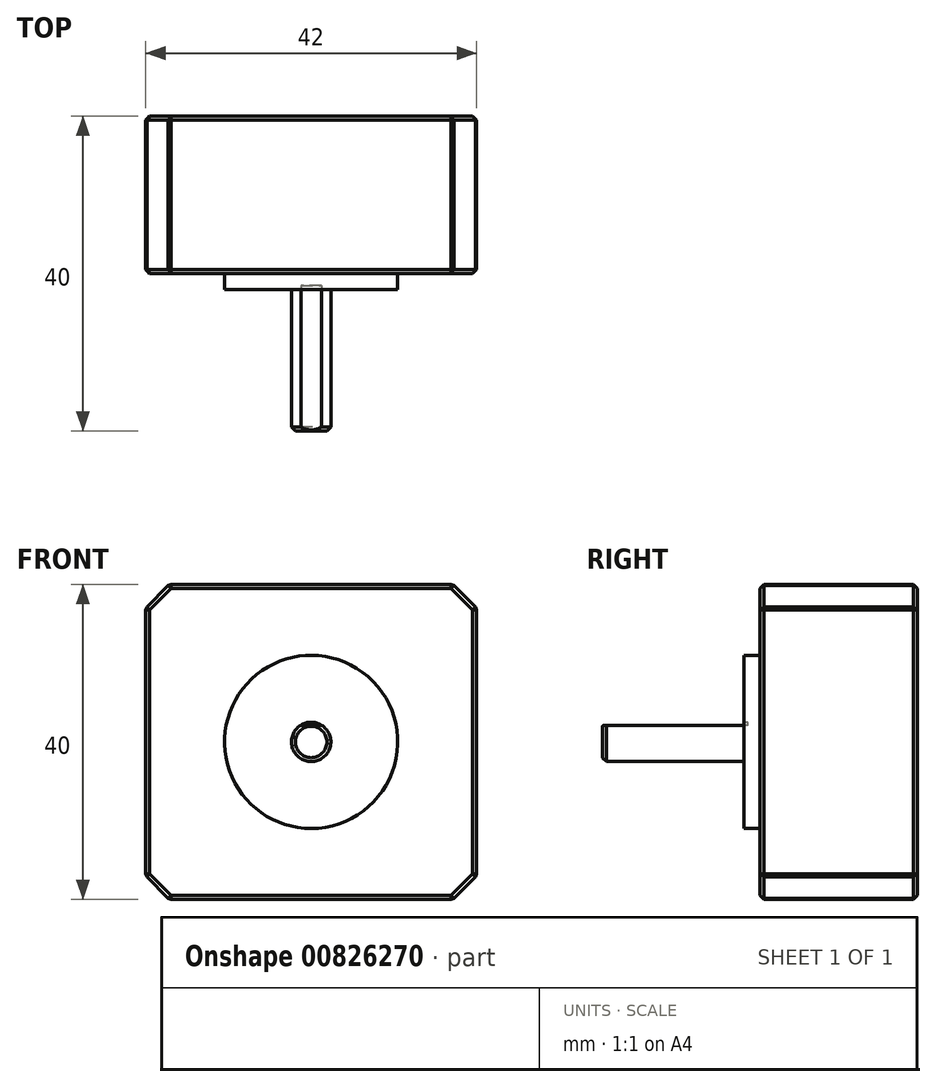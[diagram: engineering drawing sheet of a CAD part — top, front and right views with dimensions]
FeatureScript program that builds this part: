
annotation { "Feature Type Name" : "Feature", "Feature Type Description" : "" }
export const myFeature = defineFeature(function(context is Context, id is Id, definition is map)
    precondition{}
    {
        {
            var Q0;
            Q0=qCreatedBy(makeId("Front.planeOp"),FACE);
            var sketch = newSketch(context, id + "F0", { "sketchPlane" : qUnion([Q0])});
            skCircle(sketch, "E0", {"center": v(0, 0) * mm, "radius": 2.5 * mm});
            skLineSegment(sketch, "E1", {"start": v(-1.31, 2.13) * mm, "end": v(1.31, 2.13) * mm});
            skCircle(sketch, "E2", {"center": v(0, 0) * mm, "radius": 11 * mm});
            skLineSegment(sketch, "E3", {"start": v(-21, 0) * mm, "end": v(-21, 15.5) * mm});
            skLineSegment(sketch, "E4", {"start": v(-21, 15.5) * mm, "end": v(-15.5, 21) * mm});
            skLineSegment(sketch, "E5", {"start": v(-15.5, 21) * mm, "end": v(0, 21) * mm});
            skLineSegment(sketch, "E6", {"start": v(0, 0) * mm, "end": v(-21, 0) * mm, "construction": true});
            skLineSegment(sketch, "E7", {"start": v(0, 0) * mm, "end": v(0, 21) * mm, "construction": true});
            skCircle(sketch, "E8", {"center": v(-15.7, 15.69) * mm, "radius": 1.5 * mm});
            skLineSegment(sketch, "E9.MirrorCS", {"start": v(15.5, 21) * mm, "end": v(0, 21) * mm});
            skLineSegment(sketch, "E10.MirrorCS", {"start": v(21, 15.5) * mm, "end": v(15.5, 21) * mm});
            skLineSegment(sketch, "E11.MirrorCS", {"start": v(21, 0) * mm, "end": v(21, 15.5) * mm});
            skCircle(sketch, "E12.MirrorC", {"center": v(15.7, 15.69) * mm, "radius": 1.5 * mm});
            skLineSegment(sketch, "E13", {"start": v(0, 0) * mm, "end": v(21, 0) * mm, "construction": true});
            skLineSegment(sketch, "E14.MirrorCS", {"start": v(15.5, -21) * mm, "end": v(0, -21) * mm});
            skLineSegment(sketch, "E15.MirrorCS", {"start": v(21, -15.5) * mm, "end": v(15.5, -21) * mm});
            skLineSegment(sketch, "E16.MirrorCS", {"start": v(21, 0) * mm, "end": v(21, -15.5) * mm});
            skCircle(sketch, "E17.MirrorC", {"center": v(15.7, -15.69) * mm, "radius": 1.5 * mm});
            skLineSegment(sketch, "E18", {"start": v(0, -21) * mm, "end": v(0, 0) * mm, "construction": true});
            skLineSegment(sketch, "E19.MirrorCS", {"start": v(-21, 0) * mm, "end": v(-21, -15.5) * mm});
            skLineSegment(sketch, "E20.MirrorCS", {"start": v(-21, -15.5) * mm, "end": v(-15.5, -21) * mm});
            skLineSegment(sketch, "E21.MirrorCS", {"start": v(-15.5, -21) * mm, "end": v(0, -21) * mm});
            skCircle(sketch, "E22.MirrorC", {"center": v(-15.7, -15.69) * mm, "radius": 1.5 * mm});
            skLineSegment(sketch, "E23", {"start": v(0, -21.57) * mm, "end": v(0, -21) * mm});
            skLineSegment(sketch, "E24", {"start": v(0, -21.57) * mm, "end": v(-2.98, -21.57) * mm});
            skLineSegment(sketch, "E25", {"start": v(-2.98, -21.57) * mm, "end": v(-2.98, -21) * mm});
            skLineSegment(sketch, "E26", {"start": v(-2, -21.57) * mm, "end": v(-2, -29.07) * mm});
            skLineSegment(sketch, "E27", {"start": v(-2, -29.07) * mm, "end": v(-1, -29.07) * mm});
            skLineSegment(sketch, "E28", {"start": v(-1, -29.07) * mm, "end": v(-1, -21.57) * mm});
            skLineSegment(sketch, "E29", {"start": v(-1, -21.57) * mm, "end": v(0, -21.57) * mm});
            skLineSegment(sketch, "E30", {"start": v(0, -21.57) * mm, "end": v(0, -29.1) * mm});
            skLineSegment(sketch, "E31", {"start": v(0, -29.1) * mm, "end": v(-1, -29.07) * mm});
            skLineSegment(sketch, "E32.MirrorCS", {"start": v(2, -21.57) * mm, "end": v(2, -29.07) * mm});
            skLineSegment(sketch, "E33.MirrorCS", {"start": v(1, -29.07) * mm, "end": v(1, -21.57) * mm});
            skLineSegment(sketch, "E34.MirrorCS", {"start": v(2, -29.07) * mm, "end": v(1, -29.07) * mm});
            skLineSegment(sketch, "E35.MirrorCS", {"start": v(0, -29.1) * mm, "end": v(1, -29.07) * mm});
            skLineSegment(sketch, "E36.MirrorCS", {"start": v(0, -21.57) * mm, "end": v(2.98, -21.57) * mm});
            skLineSegment(sketch, "E37.MirrorCS", {"start": v(2.98, -21.57) * mm, "end": v(2.98, -21) * mm});
            skLineSegment(sketch, "E38", {"start": v(0, 0) * mm, "end": v(0, 11) * mm});
            skLineSegment(sketch, "E39", {"start": v(0, 0) * mm, "end": v(0, -2.5) * mm});
            skLineSegment(sketch, "E40", {"start": v(0, 0) * mm, "end": v(-1.31, 2.13) * mm, "construction": true});
            skLineSegment(sketch, "E41", {"start": v(0, 0) * mm, "end": v(1.31, 2.13) * mm, "construction": true});
            skSolve(sketch);
        }
        {
            var Q0;
            Q0=qCreatedBy(makeId("Right.planeOp"),FACE);
            var sketch = newSketch(context, id + "F1", { "sketchPlane" : qUnion([Q0])});
            skLineSegment(sketch, "E42", {"start": v(-6.62, 2.5) * mm, "end": v(-24.6, 2.5) * mm});
            skLineSegment(sketch, "E43", {"start": v(-24.6, 2.5) * mm, "end": v(-24.6, 0) * mm});
            skLineSegment(sketch, "E44", {"start": v(-24.6, -2.5) * mm, "end": v(-6.62, -2.5) * mm});
            skLineSegment(sketch, "E45", {"start": v(-6.62, 2.5) * mm, "end": v(-6.62, 0) * mm});
            skLineSegment(sketch, "E46", {"start": v(0, 0) * mm, "end": v(-24.6, 0) * mm, "construction": true});
            skLineSegment(sketch, "E47", {"start": v(-4.6, 20) * mm, "end": v(15.4, 20) * mm});
            skLineSegment(sketch, "E48", {"start": v(-6.6, 11) * mm, "end": v(-4.6, 11) * mm});
            skLineSegment(sketch, "E49", {"start": v(-6.6, 11) * mm, "end": v(-6.62, 2.5) * mm});
            skLineSegment(sketch, "E50", {"start": v(-4.6, 20) * mm, "end": v(-4.6, 11) * mm});
            skLineSegment(sketch, "E51", {"start": v(1, 20) * mm, "end": v(1, 13.33) * mm});
            skLineSegment(sketch, "E52", {"start": v(9.34, 20) * mm, "end": v(9.34, 13.33) * mm});
            skLineSegment(sketch, "E53", {"start": v(1, 13.33) * mm, "end": v(9.34, 13.33) * mm});
            skLineSegment(sketch, "E54", {"start": v(15.4, 0) * mm, "end": v(15.4, 20) * mm});
            skLineSegment(sketch, "E55", {"start": v(-4.6, 9.38) * mm, "end": v(1, 9.38) * mm});
            skLineSegment(sketch, "E56", {"start": v(1, 9.38) * mm, "end": v(9.34, 9.38) * mm, "construction": true});
            skLineSegment(sketch, "E57", {"start": v(9.34, 9.38) * mm, "end": v(15.4, 9.38) * mm});
            skLineSegment(sketch, "E58", {"start": v(-4.6, 11) * mm, "end": v(-4.6, 0) * mm});
            skLineSegment(sketch, "E59", {"start": v(0, 13.33) * mm, "end": v(1, 13.33) * mm});
            skLineSegment(sketch, "E60", {"start": v(0, 0) * mm, "end": v(0, 13.33) * mm});
            skLineSegment(sketch, "E61", {"start": v(9.34, 13.33) * mm, "end": v(10.34, 13.33) * mm});
            skLineSegment(sketch, "E62", {"start": v(10.34, 13.33) * mm, "end": v(10.34, 0) * mm});
            skLineSegment(sketch, "E63", {"start": v(-24.6, 0) * mm, "end": v(-24.6, -2.5) * mm});
            skLineSegment(sketch, "E64", {"start": v(-6.62, 0) * mm, "end": v(-6.62, -2.5) * mm});
            skLineSegment(sketch, "E65", {"start": v(-24.6, 0) * mm, "end": v(-6.62, 0) * mm});
            skLineSegment(sketch, "E66", {"start": v(10.34, 0) * mm, "end": v(15.4, 0) * mm});
            skLineSegment(sketch, "E67", {"start": v(-6.62, 0) * mm, "end": v(-4.6, 0) * mm});
            skLineSegment(sketch, "E68", {"start": v(0, 0) * mm, "end": v(10.34, 0) * mm});
            skLineSegment(sketch, "E69", {"start": v(-4.6, 0) * mm, "end": v(0, 0) * mm});
            skLineSegment(sketch, "E70.MirrorCS", {"start": v(-4.6, -11) * mm, "end": v(-4.6, 0) * mm});
            skLineSegment(sketch, "E71.MirrorCS", {"start": v(-4.6, -20) * mm, "end": v(-4.6, -11) * mm});
            skLineSegment(sketch, "E72.MirrorCS", {"start": v(-4.6, -9.38) * mm, "end": v(1, -9.38) * mm});
            skLineSegment(sketch, "E73.MirrorCS", {"start": v(-4.6, -20) * mm, "end": v(15.4, -20) * mm});
            skLineSegment(sketch, "E74.MirrorCS", {"start": v(1, -20) * mm, "end": v(1, -13.33) * mm});
            skLineSegment(sketch, "E75.MirrorCS", {"start": v(1, -9.38) * mm, "end": v(9.34, -9.38) * mm, "construction": true});
            skLineSegment(sketch, "E76.MirrorCS", {"start": v(1, -13.33) * mm, "end": v(9.34, -13.33) * mm});
            skLineSegment(sketch, "E77.MirrorCS", {"start": v(0, -13.33) * mm, "end": v(1, -13.33) * mm});
            skLineSegment(sketch, "E78.MirrorCS", {"start": v(0, 0) * mm, "end": v(0, -13.33) * mm});
            skLineSegment(sketch, "E79.MirrorCS", {"start": v(9.34, -13.33) * mm, "end": v(10.34, -13.33) * mm});
            skLineSegment(sketch, "E80.MirrorCS", {"start": v(10.34, -13.33) * mm, "end": v(10.34, 0) * mm});
            skLineSegment(sketch, "E81.MirrorCS", {"start": v(9.34, -20) * mm, "end": v(9.34, -13.33) * mm});
            skLineSegment(sketch, "E82.MirrorCS", {"start": v(9.34, -9.38) * mm, "end": v(15.4, -9.38) * mm});
            skLineSegment(sketch, "E83.MirrorCS", {"start": v(15.4, 0) * mm, "end": v(15.4, -20) * mm});
            skSolve(sketch);
        }
        {
            var Q0;
            Q0=makeQuery(id+"F1.imprint","IMPRINT",FACE,{"disambiguationData":[TD([[makeQuery(id+"F1.imprint","IMPRINT",EDGE,{"derivedFrom":sQuery(id+"F1.wireOp",EDGE,"E42")}),1.0]])]});
            var Q1;
            Q1=makeQuery(id+"F1.imprint","IMPRINT",FACE,{"disambiguationData":[TD([[makeQuery(id+"F1.imprint","IMPRINT",EDGE,{"derivedFrom":sQuery(id+"F1.wireOp",EDGE,"E45")}),1.0]])]});
            var Q2;
            Q2=sQuery(id+"F1.wireOp",EDGE,"E65");
            revolve(context, id + "F2", {"surfaceOperationType" : NewSurfaceOperationType.NEW, "entities" : qUnion([Q0, Q1]), "axis" : qUnion([Q2]), "revolveType" : RevolveType.FULL});
        }
        {
            var Q0;
            {var subQ0=sQuery(id+"F1.wireOp",EDGE,"E55");Q0=makeQuery(id+"F1.imprint","IMPRINT",FACE,{"disambiguationData":[TD([[makeQuery(id+"F1.imprint","IMPRINT",EDGE,{"derivedFrom":subQ0}),-1.0]])]});}
            var Q1;
            {var subQ5=sQuery(id+"F1.wireOp",EDGE,"E55");Q1=makeQuery(id+"F1.imprint","IMPRINT",FACE,{"disambiguationData":[TD([[makeQuery(id+"F1.imprint","IMPRINT",EDGE,{"derivedFrom":subQ5}),1.0]])]});}
            var Q2;
            {var subQ4=sQuery(id+"F1.wireOp",EDGE,"E53");Q2=makeQuery(id+"F1.imprint","IMPRINT",FACE,{"disambiguationData":[TD([[makeQuery(id+"F1.imprint","IMPRINT",EDGE,{"derivedFrom":subQ4}),1.0]])]});}
            var Q3;
            Q3=makeQuery(id+"F1.imprint","IMPRINT",FACE,{"disambiguationData":[TD([[makeQuery(id+"F1.imprint","IMPRINT",EDGE,{"derivedFrom":sQuery(id+"F1.wireOp",EDGE,"E53")}),-1.0]])]});
            var Q4;
            {var subQ3=sQuery(id+"F1.wireOp",EDGE,"E57");Q4=makeQuery(id+"F1.imprint","IMPRINT",FACE,{"disambiguationData":[TD([[makeQuery(id+"F1.imprint","IMPRINT",EDGE,{"derivedFrom":subQ3}),-1.0]])]});}
            var Q5;
            {var subQ5=sQuery(id+"F1.wireOp",EDGE,"E57");Q5=makeQuery(id+"F1.imprint","IMPRINT",FACE,{"disambiguationData":[TD([[makeQuery(id+"F1.imprint","IMPRINT",EDGE,{"derivedFrom":subQ5}),1.0]])]});}
            var Q6;
            Q6=makeQuery(id+"F1.imprint","IMPRINT",FACE,{"disambiguationData":[TD([[makeQuery(id+"F1.imprint","IMPRINT",EDGE,{"derivedFrom":sQuery(id+"F1.wireOp",EDGE,"E69")}),-1.0]])]});
            var Q7;
            Q7=makeQuery(id+"F1.imprint","IMPRINT",FACE,{"disambiguationData":[TD([[makeQuery(id+"F1.imprint","IMPRINT",EDGE,{"derivedFrom":sQuery(id+"F1.wireOp",EDGE,"E68")}),-1.0]])]});
            var Q8;
            {var subQ6=sQuery(id+"F1.wireOp",EDGE,"E76.MirrorCS");Q8=makeQuery(id+"F1.imprint","IMPRINT",FACE,{"disambiguationData":[TD([[makeQuery(id+"F1.imprint","IMPRINT",EDGE,{"derivedFrom":subQ6}),-1.0]])]});}
            var Q9;
            {var subQ3=sQuery(id+"F1.wireOp",EDGE,"E66");Q9=makeQuery(id+"F1.imprint","IMPRINT",FACE,{"disambiguationData":[TD([[makeQuery(id+"F1.imprint","IMPRINT",EDGE,{"derivedFrom":subQ3}),-1.0]])]});}
            var Q10;
            {var subQ5=sQuery(id+"F1.wireOp",EDGE,"E82.MirrorCS");Q10=makeQuery(id+"F1.imprint","IMPRINT",FACE,{"disambiguationData":[TD([[makeQuery(id+"F1.imprint","IMPRINT",EDGE,{"derivedFrom":subQ5}),-1.0]])]});}
            var Q11;
            {var subQ3=sQuery(id+"F1.wireOp",EDGE,"E72.MirrorCS");Q11=makeQuery(id+"F1.imprint","IMPRINT",FACE,{"disambiguationData":[TD([[makeQuery(id+"F1.imprint","IMPRINT",EDGE,{"derivedFrom":subQ3}),-1.0]])]});}
            extrude(context, id + "F3", {"entities" : qUnion([Q0, Q1, Q2, Q3, Q4, Q5, Q6, Q7, Q8, Q9, Q10, Q11]), "operationType" : NewBodyOperationType.ADD, "endBound" : BoundingType.SYMMETRIC, "depth" : 42 * mm, "offsetDistance" : 25 * mm});
        }
        {
            var Q0;
            Q0=makeQuery(id+"F3.opExtrude","CAP_EDGE",EDGE,{"disambiguationData":[OSD([sQuery(id+"F1.wireOp",EDGE,"E47")])],"isStart":true});
            var Q1;
            Q1=makeQuery(id+"F3.opExtrude","CAP_EDGE",EDGE,{"disambiguationData":[OSD([sQuery(id+"F1.wireOp",EDGE,"E47")])],"isStart":false});
            var Q2;
            Q2=makeQuery(id+"F3.opExtrude","CAP_EDGE",EDGE,{"disambiguationData":[OSD([sQuery(id+"F1.wireOp",EDGE,"E73.MirrorCS")])],"isStart":true});
            var Q3;
            Q3=makeQuery(id+"F3.opExtrude","CAP_EDGE",EDGE,{"disambiguationData":[OSD([sQuery(id+"F1.wireOp",EDGE,"E73.MirrorCS")])],"isStart":false});
            chamfer(context, id + "F4", {"entities" : qUnion([Q0, Q1, Q2, Q3]), "width" : 3 * mm, "tangentPropagation" : true});
        }
        {
            var Q0;
            Q0=makeQuery(id+"F3.opExtrude","SWEPT_EDGE",EDGE,{"disambiguationData":[OSD([sQuery(id+"F1.wireOp",EDGE,"E47"),sQuery(id+"F1.wireOp",EDGE,"E50")])]});
            var Q1;
            Q1=makeQuery(id+"F4.opChamfer","BLEND_EDGE",EDGE,{"blendedFrom":[makeQuery(id+"F3.opExtrude","CAP_EDGE",EDGE,{"disambiguationData":[OSD([sQuery(id+"F1.wireOp",EDGE,"E47")])],"isStart":false}),makeQuery(id+"F3.opExtrude","SWEPT_FACE",FACE,{"disambiguationData":[OSD([sQuery(id+"F1.wireOp",EDGE,"E50"),sQuery(id+"F1.wireOp",EDGE,"E58"),sQuery(id+"F1.wireOp",EDGE,"E70.MirrorCS"),sQuery(id+"F1.wireOp",EDGE,"E71.MirrorCS")])]})],"blendedInto":[makeQuery(id+"F3.opExtrude","SWEPT_FACE",FACE,{"disambiguationData":[OSD([sQuery(id+"F1.wireOp",EDGE,"E50"),sQuery(id+"F1.wireOp",EDGE,"E58"),sQuery(id+"F1.wireOp",EDGE,"E70.MirrorCS"),sQuery(id+"F1.wireOp",EDGE,"E71.MirrorCS")])]})]});
            var Q2;
            Q2=makeQuery(id+"F3.opExtrude","CAP_EDGE",EDGE,{"disambiguationData":[OSD([sQuery(id+"F1.wireOp",EDGE,"E50"),sQuery(id+"F1.wireOp",EDGE,"E58"),sQuery(id+"F1.wireOp",EDGE,"E70.MirrorCS"),sQuery(id+"F1.wireOp",EDGE,"E71.MirrorCS")])],"isStart":false});
            var Q3;
            Q3=makeQuery(id+"F4.opChamfer","BLEND_EDGE",EDGE,{"blendedFrom":[makeQuery(id+"F3.opExtrude","CAP_EDGE",EDGE,{"disambiguationData":[OSD([sQuery(id+"F1.wireOp",EDGE,"E73.MirrorCS")])],"isStart":false}),makeQuery(id+"F3.opExtrude","SWEPT_FACE",FACE,{"disambiguationData":[OSD([sQuery(id+"F1.wireOp",EDGE,"E50"),sQuery(id+"F1.wireOp",EDGE,"E58"),sQuery(id+"F1.wireOp",EDGE,"E70.MirrorCS"),sQuery(id+"F1.wireOp",EDGE,"E71.MirrorCS")])]})],"blendedInto":[makeQuery(id+"F3.opExtrude","SWEPT_FACE",FACE,{"disambiguationData":[OSD([sQuery(id+"F1.wireOp",EDGE,"E50"),sQuery(id+"F1.wireOp",EDGE,"E58"),sQuery(id+"F1.wireOp",EDGE,"E70.MirrorCS"),sQuery(id+"F1.wireOp",EDGE,"E71.MirrorCS")])]})]});
            var Q4;
            Q4=makeQuery(id+"F3.opExtrude","SWEPT_EDGE",EDGE,{"disambiguationData":[OSD([sQuery(id+"F1.wireOp",EDGE,"E71.MirrorCS"),sQuery(id+"F1.wireOp",EDGE,"E73.MirrorCS")])]});
            var Q5;
            Q5=makeQuery(id+"F3.opExtrude","CAP_EDGE",EDGE,{"disambiguationData":[OSD([sQuery(id+"F1.wireOp",EDGE,"E50"),sQuery(id+"F1.wireOp",EDGE,"E58"),sQuery(id+"F1.wireOp",EDGE,"E70.MirrorCS"),sQuery(id+"F1.wireOp",EDGE,"E71.MirrorCS")])],"isStart":true});
            var Q6;
            Q6=makeQuery(id+"F4.opChamfer","BLEND_EDGE",EDGE,{"blendedFrom":[makeQuery(id+"F3.opExtrude","CAP_EDGE",EDGE,{"disambiguationData":[OSD([sQuery(id+"F1.wireOp",EDGE,"E47")])],"isStart":true}),makeQuery(id+"F3.opExtrude","SWEPT_FACE",FACE,{"disambiguationData":[OSD([sQuery(id+"F1.wireOp",EDGE,"E50"),sQuery(id+"F1.wireOp",EDGE,"E58"),sQuery(id+"F1.wireOp",EDGE,"E70.MirrorCS"),sQuery(id+"F1.wireOp",EDGE,"E71.MirrorCS")])]})],"blendedInto":[makeQuery(id+"F3.opExtrude","SWEPT_FACE",FACE,{"disambiguationData":[OSD([sQuery(id+"F1.wireOp",EDGE,"E50"),sQuery(id+"F1.wireOp",EDGE,"E58"),sQuery(id+"F1.wireOp",EDGE,"E70.MirrorCS"),sQuery(id+"F1.wireOp",EDGE,"E71.MirrorCS")])]})]});
            var Q7;
            Q7=makeQuery(id+"F3.opExtrude","CAP_EDGE",EDGE,{"disambiguationData":[OSD([sQuery(id+"F1.wireOp",EDGE,"E54"),sQuery(id+"F1.wireOp",EDGE,"E83.MirrorCS")])],"isStart":false});
            var Q8;
            Q8=makeQuery(id+"F4.opChamfer","BLEND_EDGE",EDGE,{"blendedFrom":[makeQuery(id+"F3.opExtrude","CAP_EDGE",EDGE,{"disambiguationData":[OSD([sQuery(id+"F1.wireOp",EDGE,"E47")])],"isStart":false}),makeQuery(id+"F3.opExtrude","SWEPT_FACE",FACE,{"disambiguationData":[OSD([sQuery(id+"F1.wireOp",EDGE,"E54"),sQuery(id+"F1.wireOp",EDGE,"E83.MirrorCS")])]})],"blendedInto":[makeQuery(id+"F3.opExtrude","SWEPT_FACE",FACE,{"disambiguationData":[OSD([sQuery(id+"F1.wireOp",EDGE,"E54"),sQuery(id+"F1.wireOp",EDGE,"E83.MirrorCS")])]})]});
            var Q9;
            Q9=makeQuery(id+"F3.opExtrude","SWEPT_EDGE",EDGE,{"disambiguationData":[OSD([sQuery(id+"F1.wireOp",EDGE,"E47"),sQuery(id+"F1.wireOp",EDGE,"E54")])]});
            var Q10;
            Q10=makeQuery(id+"F4.opChamfer","BLEND_EDGE",EDGE,{"blendedFrom":[makeQuery(id+"F3.opExtrude","CAP_EDGE",EDGE,{"disambiguationData":[OSD([sQuery(id+"F1.wireOp",EDGE,"E47")])],"isStart":true}),makeQuery(id+"F3.opExtrude","SWEPT_FACE",FACE,{"disambiguationData":[OSD([sQuery(id+"F1.wireOp",EDGE,"E54"),sQuery(id+"F1.wireOp",EDGE,"E83.MirrorCS")])]})],"blendedInto":[makeQuery(id+"F3.opExtrude","SWEPT_FACE",FACE,{"disambiguationData":[OSD([sQuery(id+"F1.wireOp",EDGE,"E54"),sQuery(id+"F1.wireOp",EDGE,"E83.MirrorCS")])]})]});
            var Q11;
            Q11=makeQuery(id+"F3.opExtrude","CAP_EDGE",EDGE,{"disambiguationData":[OSD([sQuery(id+"F1.wireOp",EDGE,"E54"),sQuery(id+"F1.wireOp",EDGE,"E83.MirrorCS")])],"isStart":true});
            var Q12;
            Q12=makeQuery(id+"F4.opChamfer","BLEND_EDGE",EDGE,{"blendedFrom":[makeQuery(id+"F3.opExtrude","CAP_EDGE",EDGE,{"disambiguationData":[OSD([sQuery(id+"F1.wireOp",EDGE,"E73.MirrorCS")])],"isStart":true}),makeQuery(id+"F3.opExtrude","SWEPT_FACE",FACE,{"disambiguationData":[OSD([sQuery(id+"F1.wireOp",EDGE,"E54"),sQuery(id+"F1.wireOp",EDGE,"E83.MirrorCS")])]})],"blendedInto":[makeQuery(id+"F3.opExtrude","SWEPT_FACE",FACE,{"disambiguationData":[OSD([sQuery(id+"F1.wireOp",EDGE,"E54"),sQuery(id+"F1.wireOp",EDGE,"E83.MirrorCS")])]})]});
            var Q13;
            Q13=makeQuery(id+"F3.opExtrude","SWEPT_EDGE",EDGE,{"disambiguationData":[OSD([sQuery(id+"F1.wireOp",EDGE,"E73.MirrorCS"),sQuery(id+"F1.wireOp",EDGE,"E83.MirrorCS")])]});
            var Q14;
            Q14=makeQuery(id+"F4.opChamfer","BLEND_EDGE",EDGE,{"blendedFrom":[makeQuery(id+"F3.opExtrude","CAP_EDGE",EDGE,{"disambiguationData":[OSD([sQuery(id+"F1.wireOp",EDGE,"E73.MirrorCS")])],"isStart":false}),makeQuery(id+"F3.opExtrude","SWEPT_FACE",FACE,{"disambiguationData":[OSD([sQuery(id+"F1.wireOp",EDGE,"E54"),sQuery(id+"F1.wireOp",EDGE,"E83.MirrorCS")])]})],"blendedInto":[makeQuery(id+"F3.opExtrude","SWEPT_FACE",FACE,{"disambiguationData":[OSD([sQuery(id+"F1.wireOp",EDGE,"E54"),sQuery(id+"F1.wireOp",EDGE,"E83.MirrorCS")])]})]});
            var Q15;
            {var subQ0=sQuery(id+"F1.wireOp",EDGE,"E73.MirrorCS");Q15=makeQuery(id+"F4.opChamfer","BLEND_EDGE",EDGE,{"blendedFrom":[makeQuery(id+"F3.opExtrude","CAP_EDGE",EDGE,{"disambiguationData":[OSD([subQ0])],"isStart":false}),makeQuery(id+"F3.opExtrude","CAP_FACE",FACE,{"disambiguationData":[OSD([sQuery(id+"F1.wireOp",EDGE,"E47"),sQuery(id+"F1.wireOp",EDGE,"E50"),sQuery(id+"F1.wireOp",EDGE,"E54"),sQuery(id+"F1.wireOp",EDGE,"E58"),sQuery(id+"F1.wireOp",EDGE,"E70.MirrorCS"),sQuery(id+"F1.wireOp",EDGE,"E71.MirrorCS"),subQ0,sQuery(id+"F1.wireOp",EDGE,"E83.MirrorCS")])],"isStart":false})],"blendedInto":[makeQuery(id+"F3.opExtrude","CAP_FACE",FACE,{"disambiguationData":[OSD([sQuery(id+"F1.wireOp",EDGE,"E47"),sQuery(id+"F1.wireOp",EDGE,"E50"),sQuery(id+"F1.wireOp",EDGE,"E54"),sQuery(id+"F1.wireOp",EDGE,"E58"),sQuery(id+"F1.wireOp",EDGE,"E70.MirrorCS"),sQuery(id+"F1.wireOp",EDGE,"E71.MirrorCS"),subQ0,sQuery(id+"F1.wireOp",EDGE,"E83.MirrorCS")])],"isStart":false})]});}
            var Q16;
            {var subQ0=sQuery(id+"F1.wireOp",EDGE,"E73.MirrorCS");Q16=makeQuery(id+"F4.opChamfer","BLEND_EDGE",EDGE,{"blendedFrom":[makeQuery(id+"F3.opExtrude","CAP_EDGE",EDGE,{"disambiguationData":[OSD([subQ0])],"isStart":false}),makeQuery(id+"F3.opExtrude","SWEPT_FACE",FACE,{"disambiguationData":[OSD([subQ0])]})],"blendedInto":[makeQuery(id+"F3.opExtrude","SWEPT_FACE",FACE,{"disambiguationData":[OSD([subQ0])]})]});}
            var Q17;
            {var subQ0=sQuery(id+"F1.wireOp",EDGE,"E47");Q17=makeQuery(id+"F4.opChamfer","BLEND_EDGE",EDGE,{"blendedFrom":[makeQuery(id+"F3.opExtrude","CAP_EDGE",EDGE,{"disambiguationData":[OSD([subQ0])],"isStart":false}),makeQuery(id+"F3.opExtrude","CAP_FACE",FACE,{"disambiguationData":[OSD([subQ0,sQuery(id+"F1.wireOp",EDGE,"E50"),sQuery(id+"F1.wireOp",EDGE,"E54"),sQuery(id+"F1.wireOp",EDGE,"E58"),sQuery(id+"F1.wireOp",EDGE,"E70.MirrorCS"),sQuery(id+"F1.wireOp",EDGE,"E71.MirrorCS"),sQuery(id+"F1.wireOp",EDGE,"E73.MirrorCS"),sQuery(id+"F1.wireOp",EDGE,"E83.MirrorCS")])],"isStart":false})],"blendedInto":[makeQuery(id+"F3.opExtrude","CAP_FACE",FACE,{"disambiguationData":[OSD([subQ0,sQuery(id+"F1.wireOp",EDGE,"E50"),sQuery(id+"F1.wireOp",EDGE,"E54"),sQuery(id+"F1.wireOp",EDGE,"E58"),sQuery(id+"F1.wireOp",EDGE,"E70.MirrorCS"),sQuery(id+"F1.wireOp",EDGE,"E71.MirrorCS"),sQuery(id+"F1.wireOp",EDGE,"E73.MirrorCS"),sQuery(id+"F1.wireOp",EDGE,"E83.MirrorCS")])],"isStart":false})]});}
            var Q18;
            {var subQ0=sQuery(id+"F1.wireOp",EDGE,"E47");Q18=makeQuery(id+"F4.opChamfer","BLEND_EDGE",EDGE,{"blendedFrom":[makeQuery(id+"F3.opExtrude","CAP_EDGE",EDGE,{"disambiguationData":[OSD([subQ0])],"isStart":false}),makeQuery(id+"F3.opExtrude","SWEPT_FACE",FACE,{"disambiguationData":[OSD([subQ0])]})],"blendedInto":[makeQuery(id+"F3.opExtrude","SWEPT_FACE",FACE,{"disambiguationData":[OSD([subQ0])]})]});}
            var Q19;
            {var subQ0=sQuery(id+"F1.wireOp",EDGE,"E47");Q19=makeQuery(id+"F4.opChamfer","BLEND_EDGE",EDGE,{"blendedFrom":[makeQuery(id+"F3.opExtrude","CAP_EDGE",EDGE,{"disambiguationData":[OSD([subQ0])],"isStart":true}),makeQuery(id+"F3.opExtrude","SWEPT_FACE",FACE,{"disambiguationData":[OSD([subQ0])]})],"blendedInto":[makeQuery(id+"F3.opExtrude","SWEPT_FACE",FACE,{"disambiguationData":[OSD([subQ0])]})]});}
            var Q20;
            {var subQ0=sQuery(id+"F1.wireOp",EDGE,"E47");Q20=makeQuery(id+"F4.opChamfer","BLEND_EDGE",EDGE,{"blendedFrom":[makeQuery(id+"F3.opExtrude","CAP_EDGE",EDGE,{"disambiguationData":[OSD([subQ0])],"isStart":true}),makeQuery(id+"F3.opExtrude","CAP_FACE",FACE,{"disambiguationData":[OSD([subQ0,sQuery(id+"F1.wireOp",EDGE,"E50"),sQuery(id+"F1.wireOp",EDGE,"E54"),sQuery(id+"F1.wireOp",EDGE,"E58"),sQuery(id+"F1.wireOp",EDGE,"E70.MirrorCS"),sQuery(id+"F1.wireOp",EDGE,"E71.MirrorCS"),sQuery(id+"F1.wireOp",EDGE,"E73.MirrorCS"),sQuery(id+"F1.wireOp",EDGE,"E83.MirrorCS")])],"isStart":true})],"blendedInto":[makeQuery(id+"F3.opExtrude","CAP_FACE",FACE,{"disambiguationData":[OSD([subQ0,sQuery(id+"F1.wireOp",EDGE,"E50"),sQuery(id+"F1.wireOp",EDGE,"E54"),sQuery(id+"F1.wireOp",EDGE,"E58"),sQuery(id+"F1.wireOp",EDGE,"E70.MirrorCS"),sQuery(id+"F1.wireOp",EDGE,"E71.MirrorCS"),sQuery(id+"F1.wireOp",EDGE,"E73.MirrorCS"),sQuery(id+"F1.wireOp",EDGE,"E83.MirrorCS")])],"isStart":true})]});}
            var Q21;
            {var subQ0=sQuery(id+"F1.wireOp",EDGE,"E73.MirrorCS");Q21=makeQuery(id+"F4.opChamfer","BLEND_EDGE",EDGE,{"blendedFrom":[makeQuery(id+"F3.opExtrude","CAP_EDGE",EDGE,{"disambiguationData":[OSD([subQ0])],"isStart":true}),makeQuery(id+"F3.opExtrude","CAP_FACE",FACE,{"disambiguationData":[OSD([sQuery(id+"F1.wireOp",EDGE,"E47"),sQuery(id+"F1.wireOp",EDGE,"E50"),sQuery(id+"F1.wireOp",EDGE,"E54"),sQuery(id+"F1.wireOp",EDGE,"E58"),sQuery(id+"F1.wireOp",EDGE,"E70.MirrorCS"),sQuery(id+"F1.wireOp",EDGE,"E71.MirrorCS"),subQ0,sQuery(id+"F1.wireOp",EDGE,"E83.MirrorCS")])],"isStart":true})],"blendedInto":[makeQuery(id+"F3.opExtrude","CAP_FACE",FACE,{"disambiguationData":[OSD([sQuery(id+"F1.wireOp",EDGE,"E47"),sQuery(id+"F1.wireOp",EDGE,"E50"),sQuery(id+"F1.wireOp",EDGE,"E54"),sQuery(id+"F1.wireOp",EDGE,"E58"),sQuery(id+"F1.wireOp",EDGE,"E70.MirrorCS"),sQuery(id+"F1.wireOp",EDGE,"E71.MirrorCS"),subQ0,sQuery(id+"F1.wireOp",EDGE,"E83.MirrorCS")])],"isStart":true})]});}
            var Q22;
            {var subQ0=sQuery(id+"F1.wireOp",EDGE,"E73.MirrorCS");Q22=makeQuery(id+"F4.opChamfer","BLEND_EDGE",EDGE,{"blendedFrom":[makeQuery(id+"F3.opExtrude","CAP_EDGE",EDGE,{"disambiguationData":[OSD([subQ0])],"isStart":true}),makeQuery(id+"F3.opExtrude","SWEPT_FACE",FACE,{"disambiguationData":[OSD([subQ0])]})],"blendedInto":[makeQuery(id+"F3.opExtrude","SWEPT_FACE",FACE,{"disambiguationData":[OSD([subQ0])]})]});}
            var Q23;
            Q23=makeQuery(id+"F4.opChamfer","BLEND_EDGE",EDGE,{"blendedFrom":[makeQuery(id+"F3.opExtrude","CAP_EDGE",EDGE,{"disambiguationData":[OSD([sQuery(id+"F1.wireOp",EDGE,"E73.MirrorCS")])],"isStart":true}),makeQuery(id+"F3.opExtrude","SWEPT_FACE",FACE,{"disambiguationData":[OSD([sQuery(id+"F1.wireOp",EDGE,"E50"),sQuery(id+"F1.wireOp",EDGE,"E58"),sQuery(id+"F1.wireOp",EDGE,"E70.MirrorCS"),sQuery(id+"F1.wireOp",EDGE,"E71.MirrorCS")])]})],"blendedInto":[makeQuery(id+"F3.opExtrude","SWEPT_FACE",FACE,{"disambiguationData":[OSD([sQuery(id+"F1.wireOp",EDGE,"E50"),sQuery(id+"F1.wireOp",EDGE,"E58"),sQuery(id+"F1.wireOp",EDGE,"E70.MirrorCS"),sQuery(id+"F1.wireOp",EDGE,"E71.MirrorCS")])]})]});
            var Q24;
            Q24=makeQuery(id+"F2.opRevolve","SWEPT_EDGE",EDGE,{"disambiguationData":[OSD([sQuery(id+"F1.wireOp",EDGE,"E42"),sQuery(id+"F1.wireOp",EDGE,"E43")])]});
            chamfer(context, id + "F5", {"entities" : qUnion([Q0, Q1, Q2, Q3, Q4, Q5, Q6, Q7, Q8, Q9, Q10, Q11, Q12, Q13, Q14, Q15, Q16, Q17, Q18, Q19, Q20, Q21, Q22, Q23, Q24]), "width" : 0.5 * mm, "tangentPropagation" : true});
        }
        {
            var Q0;
            Q0=makeQuery(id+"F2.opRevolve","SWEPT_FACE",FACE,{"disambiguationData":[OSD([sQuery(id+"F1.wireOp",EDGE,"E43")])]});
            var sketch = newSketch(context, id + "F6", { "sketchPlane" : qUnion([Q0])});
            skLineSegment(sketch, "E84.0", {"start": v(-1.31, 2.13) * mm, "end": v(1.31, 2.13) * mm});
            skCircle(sketch, "E85.0", {"center": v(0, 0) * mm, "radius": 2.5 * mm});
            skLineSegment(sketch, "E86", {"start": v(1.31, 2.13) * mm, "end": v(1.31, 2.13) * mm});
            skSolve(sketch);
        }
        {
            var Q0;
            {var subQ0=sQuery(id+"F6.wireOp",EDGE,"E84.0");Q0=makeQuery(id+"F6.imprint","IMPRINT",FACE,{"disambiguationData":[TD([[makeQuery(id+"F6.imprint","IMPRINT",EDGE,{"derivedFrom":subQ0}),1.0]])]});}
            extrude(context, id + "F7", {"entities" : qUnion([Q0]), "operationType" : NewBodyOperationType.REMOVE, "oppositeDirection" : true, "depth" : 18.5 * mm, "offsetDistance" : 25 * mm});
        }
    });
